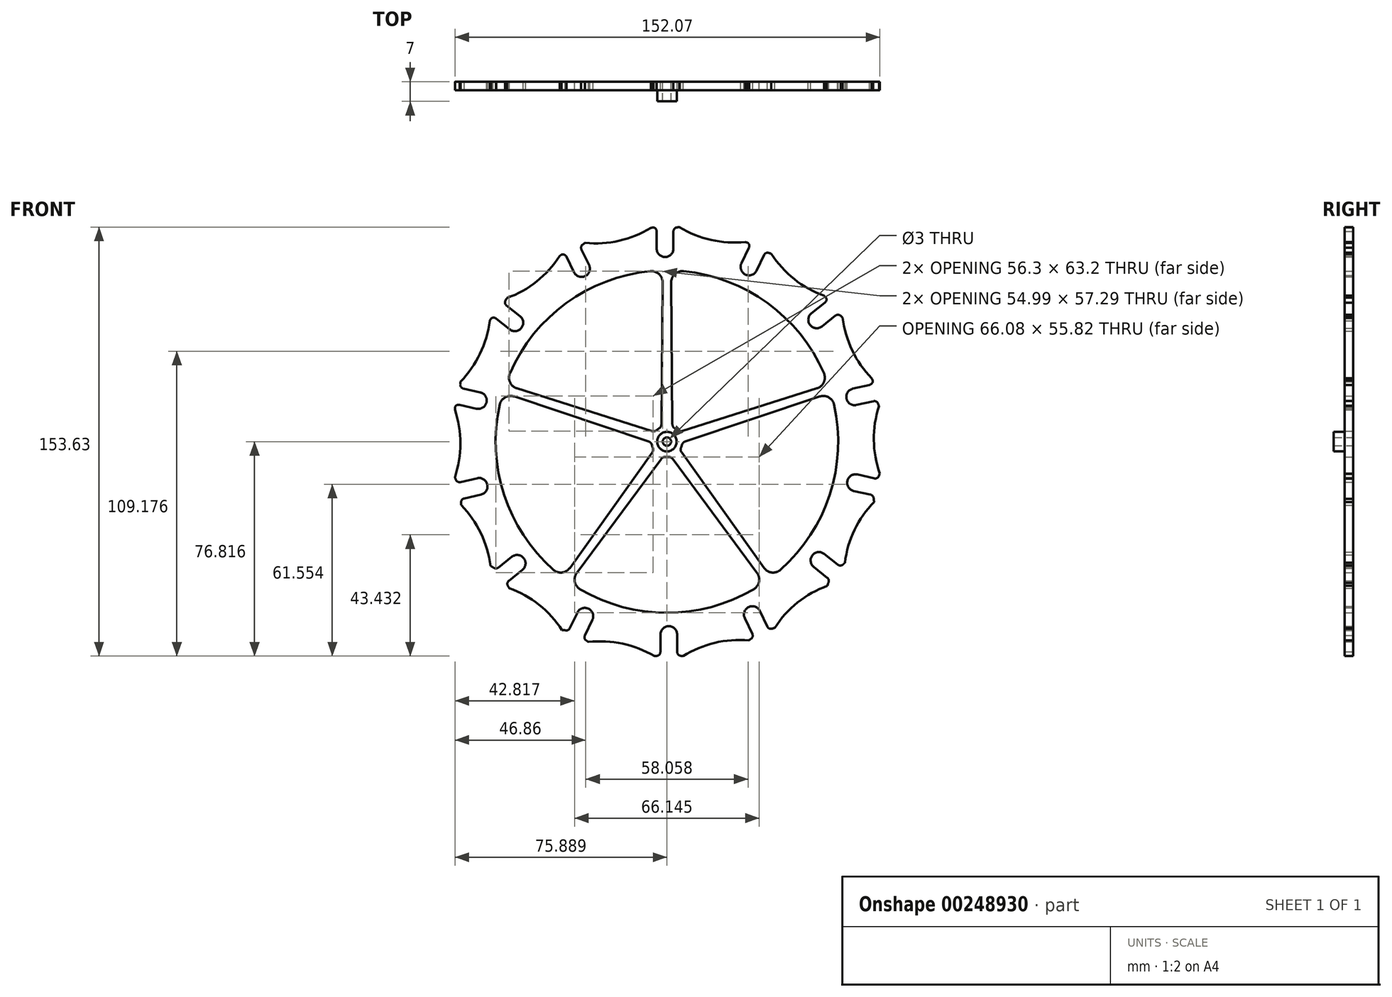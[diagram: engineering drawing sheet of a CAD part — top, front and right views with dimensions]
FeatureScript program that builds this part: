
annotation { "Feature Type Name" : "Feature", "Feature Type Description" : "" }
export const myFeature = defineFeature(function(context is Context, id is Id, definition is map)
    precondition{}
    {
        {
            var Q0;
            Q0=qCreatedBy(makeId("Front.planeOp"),FACE);
            var sketch = newSketch(context, id + "F0", { "sketchPlane" : qUnion([Q0])});
            skCircle(sketch, "E0", {"center": v(-22.2, -31.98) * mm, "radius": 2 * mm});
            skCircle(sketch, "E1", {"center": v(-22.2, -71.34) * mm, "radius": 1.5 * mm});
            skPoint(sketch, "E2.startSnap0", {"position": v(-22.24, -28.34) * mm});
            skPoint(sketch, "E3.orphan", {"position": v(-21.48, -28.34) * mm});
            skCircle(sketch, "E4", {"center": v(-22.2, -71.34) * mm, "radius": 2.5 * mm});
            skArc(sketch, "E5", {"start": v(-26.44, -36.03) * mm, "mid": v(-26.89, -36.09) * mm, "end": v(-27.34, -36.15) * mm});
            skArc(sketch, "E6.1.1", {"start": v(7.2, -29.99) * mm, "mid": v(6.81, -30.23) * mm, "end": v(6.43, -30.49) * mm});
            skArc(sketch, "E6.2.1", {"start": v(34.87, -9.95) * mm, "mid": v(34.73, -10.46) * mm, "end": v(34.6, -10.96) * mm});
            skArc(sketch, "E6.4.1", {"start": v(52.7, 54.24) * mm, "mid": v(52.87, 53.82) * mm, "end": v(53.03, 53.4) * mm});
            skPoint(sketch, "E6.center", {"position": v(-22.86, 40.67) * mm});
            skLineSegment(sketch, "E7", {"start": v(-25.2, -28.42) * mm, "end": v(-25.2, -34.62) * mm});
            skLineSegment(sketch, "E8.MirrorCS", {"start": v(-19.2, -28.42) * mm, "end": v(-19.2, -34.6) * mm});
            skArc(sketch, "E9", {"start": v(-19.2, -28.42) * mm, "mid": v(-22.2, -25.42) * mm, "end": v(-25.2, -28.42) * mm});
            skPoint(sketch, "E10.orphan", {"position": v(-25.2, -27.08) * mm});
            skPoint(sketch, "E11.orphan", {"position": v(-19.2, -27.02) * mm});
            skArc(sketch, "E12", {"start": v(-26.44, -36.03) * mm, "mid": v(-25.55, -35.56) * mm, "end": v(-25.2, -34.62) * mm});
            skPoint(sketch, "E13.orphan", {"position": v(-25.2, -35.93) * mm});
            skArc(sketch, "E14.MirrorCS", {"start": v(-17.94, -36.03) * mm, "mid": v(-18.84, -35.55) * mm, "end": v(-19.2, -34.6) * mm});
            skArc(sketch, "E15.1.0", {"start": v(10.42, -19.99) * mm, "mid": v(6.42, -18.59) * mm, "end": v(5.02, -22.6) * mm});
            skLineSegment(sketch, "E15.1.1", {"start": v(5.02, -22.6) * mm, "end": v(7.7, -28.18) * mm});
            skArc(sketch, "E15.1.2", {"start": v(7.2, -29.99) * mm, "mid": v(7.8, -29.18) * mm, "end": v(7.7, -28.18) * mm});
            skArc(sketch, "E15.1.3", {"start": v(14.85, -26.3) * mm, "mid": v(13.83, -26.26) * mm, "end": v(13.1, -25.55) * mm});
            skLineSegment(sketch, "E15.1.4", {"start": v(10.42, -19.99) * mm, "end": v(13.1, -25.55) * mm});
            skArc(sketch, "E15.2.0", {"start": v(33.44, 0.46) * mm, "mid": v(29.23, -0.01) * mm, "end": v(29.7, -4.23) * mm});
            skLineSegment(sketch, "E15.2.1", {"start": v(29.7, -4.23) * mm, "end": v(34.55, -8.1) * mm});
            skArc(sketch, "E15.2.2", {"start": v(34.87, -9.95) * mm, "mid": v(35.06, -8.96) * mm, "end": v(34.55, -8.1) * mm});
            skArc(sketch, "E15.2.3", {"start": v(40.17, -3.3) * mm, "mid": v(39.23, -3.72) * mm, "end": v(38.27, -3.39) * mm});
            skLineSegment(sketch, "E15.2.4", {"start": v(33.44, 0.46) * mm, "end": v(38.27, -3.39) * mm});
            skArc(sketch, "E15.3.0", {"start": v(45.31, 28.87) * mm, "mid": v(41.72, 26.61) * mm, "end": v(43.98, 23.02) * mm});
            skLineSegment(sketch, "E15.3.1", {"start": v(43.98, 23.02) * mm, "end": v(50.02, 21.64) * mm});
            skArc(sketch, "E15.3.2", {"start": v(51.12, 20.11) * mm, "mid": v(50.86, 21.08) * mm, "end": v(50.02, 21.64) * mm});
            skArc(sketch, "E15.3.3", {"start": v(53, 28.4) * mm, "mid": v(52.34, 27.62) * mm, "end": v(51.33, 27.5) * mm});
            skLineSegment(sketch, "E15.3.4", {"start": v(45.31, 28.87) * mm, "end": v(51.33, 27.5) * mm});
            skArc(sketch, "E15.4.0", {"start": v(43.68, 59.62) * mm, "mid": v(41.42, 56.02) * mm, "end": v(45.01, 53.77) * mm});
            skLineSegment(sketch, "E15.4.1", {"start": v(45.01, 53.77) * mm, "end": v(51.06, 55.15) * mm});
            skArc(sketch, "E15.4.2", {"start": v(52.7, 54.24) * mm, "mid": v(52.06, 55) * mm, "end": v(51.06, 55.15) * mm});
            skArc(sketch, "E15.4.3", {"start": v(50.82, 62.53) * mm, "mid": v(50.55, 61.54) * mm, "end": v(49.7, 61) * mm});
            skLineSegment(sketch, "E15.4.4", {"start": v(43.68, 59.62) * mm, "end": v(49.7, 61) * mm});
            skArc(sketch, "E15.5.0", {"start": v(28.87, 86.6) * mm, "mid": v(28.4, 82.4) * mm, "end": v(32.6, 81.92) * mm});
            skLineSegment(sketch, "E15.5.1", {"start": v(32.6, 81.92) * mm, "end": v(37.46, 85.79) * mm});
            skArc(sketch, "E15.5.2", {"start": v(39.33, 85.69) * mm, "mid": v(38.41, 86.1) * mm, "end": v(37.46, 85.79) * mm});
            skArc(sketch, "E15.5.3", {"start": v(34.04, 92.33) * mm, "mid": v(34.23, 91.33) * mm, "end": v(33.7, 90.46) * mm});
            skLineSegment(sketch, "E15.5.4", {"start": v(28.87, 86.6) * mm, "end": v(33.7, 90.46) * mm});
            skArc(sketch, "E15.6.0", {"start": v(3.8, 104.5) * mm, "mid": v(5.2, 100.5) * mm, "end": v(9.21, 101.9) * mm});
            skLineSegment(sketch, "E15.6.1", {"start": v(9.21, 101.9) * mm, "end": v(11.9, 107.49) * mm});
            skArc(sketch, "E15.6.2", {"start": v(13.64, 108.21) * mm, "mid": v(12.63, 108.18) * mm, "end": v(11.9, 107.49) * mm});
            skArc(sketch, "E15.6.3", {"start": v(5.99, 111.9) * mm, "mid": v(6.6, 111.08) * mm, "end": v(6.49, 110.06) * mm});
            skLineSegment(sketch, "E15.6.4", {"start": v(3.8, 104.5) * mm, "end": v(6.49, 110.06) * mm});
            skArc(sketch, "E15.7.0", {"start": v(-26.53, 109.75) * mm, "mid": v(-23.53, 106.75) * mm, "end": v(-20.53, 109.75) * mm});
            skLineSegment(sketch, "E15.7.1", {"start": v(-20.53, 109.75) * mm, "end": v(-20.53, 115.96) * mm});
            skArc(sketch, "E15.7.2", {"start": v(-19.28, 117.36) * mm, "mid": v(-20.17, 116.9) * mm, "end": v(-20.53, 115.96) * mm});
            skArc(sketch, "E15.7.3", {"start": v(-27.78, 117.36) * mm, "mid": v(-26.88, 116.88) * mm, "end": v(-26.53, 115.92) * mm});
            skLineSegment(sketch, "E15.7.4", {"start": v(-26.53, 109.75) * mm, "end": v(-26.53, 115.92) * mm});
            skArc(sketch, "E15.8.0", {"start": v(-56.14, 101.32) * mm, "mid": v(-52.14, 99.92) * mm, "end": v(-50.74, 103.92) * mm});
            skLineSegment(sketch, "E15.8.1", {"start": v(-50.74, 103.92) * mm, "end": v(-53.43, 109.51) * mm});
            skArc(sketch, "E15.8.2", {"start": v(-52.92, 111.32) * mm, "mid": v(-53.51, 110.51) * mm, "end": v(-53.43, 109.51) * mm});
            skArc(sketch, "E15.8.3", {"start": v(-60.57, 107.63) * mm, "mid": v(-59.55, 107.6) * mm, "end": v(-58.82, 106.88) * mm});
            skLineSegment(sketch, "E15.8.4", {"start": v(-56.14, 101.32) * mm, "end": v(-58.82, 106.88) * mm});
            skArc(sketch, "E15.9.0", {"start": v(-79.16, 80.87) * mm, "mid": v(-74.95, 81.35) * mm, "end": v(-75.42, 85.56) * mm});
            skLineSegment(sketch, "E15.9.1", {"start": v(-75.42, 85.56) * mm, "end": v(-80.27, 89.43) * mm});
            skArc(sketch, "E15.9.2", {"start": v(-80.6, 91.28) * mm, "mid": v(-80.78, 90.3) * mm, "end": v(-80.27, 89.43) * mm});
            skArc(sketch, "E15.9.3", {"start": v(-85.9, 84.64) * mm, "mid": v(-84.95, 85.05) * mm, "end": v(-83.99, 84.72) * mm});
            skLineSegment(sketch, "E15.9.4", {"start": v(-79.16, 80.87) * mm, "end": v(-83.99, 84.72) * mm});
            skArc(sketch, "E15.10.0", {"start": v(-91.03, 52.46) * mm, "mid": v(-87.44, 54.72) * mm, "end": v(-89.7, 58.31) * mm});
            skLineSegment(sketch, "E15.10.1", {"start": v(-89.7, 58.31) * mm, "end": v(-95.74, 59.7) * mm});
            skArc(sketch, "E15.10.2", {"start": v(-96.84, 61.22) * mm, "mid": v(-96.58, 60.25) * mm, "end": v(-95.74, 59.7) * mm});
            skArc(sketch, "E15.10.3", {"start": v(-98.73, 52.94) * mm, "mid": v(-98.06, 53.7) * mm, "end": v(-97.05, 53.83) * mm});
            skLineSegment(sketch, "E15.10.4", {"start": v(-91.03, 52.46) * mm, "end": v(-97.05, 53.83) * mm});
            skArc(sketch, "E15.11.0", {"start": v(-89.4, 21.71) * mm, "mid": v(-87.14, 25.3) * mm, "end": v(-90.73, 27.56) * mm});
            skLineSegment(sketch, "E15.11.1", {"start": v(-90.73, 27.56) * mm, "end": v(-96.78, 26.18) * mm});
            skArc(sketch, "E15.11.2", {"start": v(-98.43, 27.09) * mm, "mid": v(-97.78, 26.32) * mm, "end": v(-96.78, 26.18) * mm});
            skArc(sketch, "E15.11.3", {"start": v(-96.54, 18.8) * mm, "mid": v(-96.27, 19.79) * mm, "end": v(-95.42, 20.34) * mm});
            skLineSegment(sketch, "E15.11.4", {"start": v(-89.4, 21.71) * mm, "end": v(-95.42, 20.34) * mm});
            skArc(sketch, "E15.12.0", {"start": v(-74.59, -5.28) * mm, "mid": v(-74.11, -1.06) * mm, "end": v(-78.33, -0.59) * mm});
            skLineSegment(sketch, "E15.12.1", {"start": v(-78.33, -0.59) * mm, "end": v(-83.18, -4.46) * mm});
            skArc(sketch, "E15.12.2", {"start": v(-85.05, -4.36) * mm, "mid": v(-84.13, -4.76) * mm, "end": v(-83.18, -4.46) * mm});
            skArc(sketch, "E15.12.3", {"start": v(-79.76, -11) * mm, "mid": v(-79.95, -10) * mm, "end": v(-79.41, -9.13) * mm});
            skLineSegment(sketch, "E15.12.4", {"start": v(-74.59, -5.28) * mm, "end": v(-79.41, -9.13) * mm});
            skArc(sketch, "E15.13.0", {"start": v(-49.53, -23.17) * mm, "mid": v(-50.93, -19.17) * mm, "end": v(-54.94, -20.57) * mm});
            skLineSegment(sketch, "E15.13.1", {"start": v(-54.94, -20.57) * mm, "end": v(-57.63, -26.16) * mm});
            skArc(sketch, "E15.13.2", {"start": v(-59.36, -26.88) * mm, "mid": v(-58.36, -26.85) * mm, "end": v(-57.63, -26.16) * mm});
            skArc(sketch, "E15.13.3", {"start": v(-51.7, -30.57) * mm, "mid": v(-52.31, -29.75) * mm, "end": v(-52.2, -28.73) * mm});
            skLineSegment(sketch, "E15.13.4", {"start": v(-49.53, -23.17) * mm, "end": v(-52.2, -28.73) * mm});
            skPoint(sketch, "E16.trimOffspring.start.orphan", {"position": v(-19.2, -35.87) * mm});
            skPoint(sketch, "E17.orphan", {"position": v(-11.1, -37.55) * mm});
            skArc(sketch, "E18.trimOffspring", {"start": v(6.43, -30.49) * mm, "mid": v(-5.77, -31.4) * mm, "end": v(-17.04, -36.15) * mm});
            skArc(sketch, "E19.trimOffspring", {"start": v(15.71, -26.02) * mm, "mid": v(15.28, -26.16) * mm, "end": v(14.85, -26.3) * mm});
            skArc(sketch, "E20.trimOffspring", {"start": v(34.6, -10.96) * mm, "mid": v(23.92, -16.95) * mm, "end": v(15.71, -26.02) * mm});
            skArc(sketch, "E21.trimOffspring", {"start": v(40.83, -2.68) * mm, "mid": v(40.5, -3) * mm, "end": v(40.17, -3.3) * mm});
            skArc(sketch, "E22.trimOffspring", {"start": v(51.12, 20.11) * mm, "mid": v(51.2, 19.6) * mm, "end": v(51.3, 19.08) * mm});
            skArc(sketch, "E23.trimOffspring", {"start": v(53.32, 29.25) * mm, "mid": v(53.16, 28.82) * mm, "end": v(53, 28.4) * mm});
            skArc(sketch, "E24.trimOffspring", {"start": v(51.3, 19.08) * mm, "mid": v(44.29, 9.05) * mm, "end": v(40.83, -2.68) * mm});
            skArc(sketch, "E25.trimOffspring", {"start": v(53.03, 53.4) * mm, "mid": v(51.2, 41.3) * mm, "end": v(53.32, 29.25) * mm});
            skArc(sketch, "E26.trimOffspring", {"start": v(50.47, 63.3) * mm, "mid": v(50.64, 62.91) * mm, "end": v(50.82, 62.53) * mm});
            skArc(sketch, "E27.trimOffspring", {"start": v(39.99, 85.06) * mm, "mid": v(43.45, 73.32) * mm, "end": v(50.47, 63.3) * mm});
            skArc(sketch, "E28.trimOffspring", {"start": v(33.38, 92.88) * mm, "mid": v(33.7, 92.6) * mm, "end": v(34.04, 92.33) * mm});
            skArc(sketch, "E29.trimOffspring", {"start": v(13.64, 108.21) * mm, "mid": v(14.07, 108.07) * mm, "end": v(14.5, 107.93) * mm});
            skArc(sketch, "E30.trimOffspring", {"start": v(14.5, 107.93) * mm, "mid": v(22.71, 98.86) * mm, "end": v(33.38, 92.88) * mm});
            skArc(sketch, "E31.trimOffspring", {"start": v(5.16, 112.1) * mm, "mid": v(5.57, 112) * mm, "end": v(5.99, 111.9) * mm});
            skArc(sketch, "E32.trimOffspring", {"start": v(-19.28, 117.36) * mm, "mid": v(-18.83, 117.42) * mm, "end": v(-18.38, 117.48) * mm});
            skArc(sketch, "E33.trimOffspring", {"start": v(-18.38, 117.48) * mm, "mid": v(-7.05, 112.87) * mm, "end": v(5.16, 112.1) * mm});
            skArc(sketch, "E34.trimOffspring", {"start": v(-28.61, 117.2) * mm, "mid": v(-28.2, 117.27) * mm, "end": v(-27.78, 117.36) * mm});
            skArc(sketch, "E35.trimOffspring", {"start": v(-52.92, 111.32) * mm, "mid": v(-52.53, 111.57) * mm, "end": v(-52.15, 111.82) * mm});
            skArc(sketch, "E36.trimOffspring", {"start": v(-52.15, 111.82) * mm, "mid": v(-39.95, 112.58) * mm, "end": v(-28.61, 117.2) * mm});
            skArc(sketch, "E37.trimOffspring", {"start": v(-61.25, 107.12) * mm, "mid": v(-60.9, 107.37) * mm, "end": v(-60.57, 107.63) * mm});
            skArc(sketch, "E38.trimOffspring", {"start": v(-80.6, 91.28) * mm, "mid": v(-80.36, 91.67) * mm, "end": v(-80.13, 92.06) * mm});
            skArc(sketch, "E39.trimOffspring", {"start": v(-80.13, 92.06) * mm, "mid": v(-69.46, 98.05) * mm, "end": v(-61.25, 107.12) * mm});
            skArc(sketch, "E40.trimOffspring", {"start": v(-86.28, 83.88) * mm, "mid": v(-86.08, 84.26) * mm, "end": v(-85.9, 84.64) * mm});
            skArc(sketch, "E41.trimOffspring", {"start": v(-96.84, 61.22) * mm, "mid": v(-96.8, 61.67) * mm, "end": v(-96.75, 62.13) * mm});
            skArc(sketch, "E42.trimOffspring", {"start": v(-96.75, 62.13) * mm, "mid": v(-89.74, 72.15) * mm, "end": v(-86.28, 83.88) * mm});
            skArc(sketch, "E43.trimOffspring", {"start": v(-98.75, 52.09) * mm, "mid": v(-98.74, 52.51) * mm, "end": v(-98.73, 52.94) * mm});
            skArc(sketch, "E44.trimOffspring", {"start": v(-98.43, 27.09) * mm, "mid": v(-98.59, 27.51) * mm, "end": v(-98.75, 27.94) * mm});
            skArc(sketch, "E45.trimOffspring", {"start": v(-98.75, 27.94) * mm, "mid": v(-96.78, 40.01) * mm, "end": v(-98.75, 52.09) * mm});
            skArc(sketch, "E46.trimOffspring", {"start": v(-96.46, 17.9) * mm, "mid": v(-96.5, 18.35) * mm, "end": v(-96.54, 18.8) * mm});
            skArc(sketch, "E47.trimOffspring", {"start": v(-85.05, -4.36) * mm, "mid": v(-85.52, -4.1) * mm, "end": v(-85.98, -3.86) * mm});
            skArc(sketch, "E48.trimOffspring", {"start": v(-85.98, -3.86) * mm, "mid": v(-89.44, 7.88) * mm, "end": v(-96.46, 17.9) * mm});
            skArc(sketch, "E49.trimOffspring", {"start": v(-79.29, -11.78) * mm, "mid": v(-79.52, -11.39) * mm, "end": v(-79.76, -11) * mm});
            skArc(sketch, "E50.trimOffspring", {"start": v(-60.41, -26.83) * mm, "mid": v(-68.62, -17.76) * mm, "end": v(-79.29, -11.78) * mm});
            skArc(sketch, "E51.trimOffspring", {"start": v(-59.36, -26.88) * mm, "mid": v(-59.89, -26.85) * mm, "end": v(-60.41, -26.83) * mm});
            skArc(sketch, "E52.trimOffspring", {"start": v(-50.95, -31.07) * mm, "mid": v(-51.33, -30.82) * mm, "end": v(-51.7, -30.57) * mm});
            skArc(sketch, "E53.trimOffspring", {"start": v(-27.34, -36.15) * mm, "mid": v(-38.73, -31.68) * mm, "end": v(-50.95, -31.07) * mm});
            skArc(sketch, "E54.trimOffspring", {"start": v(-17.04, -36.15) * mm, "mid": v(-17.5, -36.09) * mm, "end": v(-17.94, -36.03) * mm});
            skPoint(sketch, "E55.orphan", {"position": v(-33.29, -37.55) * mm});
            skLineSegment(sketch, "E56", {"start": v(39.33, 85.69) * mm, "end": v(39.99, 85.06) * mm});
            skCircle(sketch, "E57", {"center": v(-22.86, 40.67) * mm, "radius": 1.5 * mm});
            skCircle(sketch, "E58", {"center": v(-22.86, 40.67) * mm, "radius": 3.5 * mm});
            skArc(sketch, "E59", {"start": v(-28.22, 39.42) * mm, "mid": v(-28.1, 38.97) * mm, "end": v(-27.93, 38.53) * mm});
            skLineSegment(sketch, "E60", {"start": v(-23.53, 110.93) * mm, "end": v(-23.53, 109.75) * mm});
            skArc(sketch, "E61", {"start": v(-82.71, 53.89) * mm, "mid": v(-81.15, 21.73) * mm, "end": v(-63.5, -5.2) * mm});
            skLineSegment(sketch, "E62", {"start": v(-24.82, 46.93) * mm, "end": v(-24.4, 97.66) * mm});
            skLineSegment(sketch, "E63.trimOffspring", {"start": v(-23.53, 109.75) * mm, "end": v(-23.53, 110.93) * mm});
            skLineSegment(sketch, "E64.MirrorCS", {"start": v(-20.9, 46.93) * mm, "end": v(-21.33, 97.66) * mm});
            skLineSegment(sketch, "E65.MirrorCS", {"start": v(-20.74, 35.68) * mm, "end": v(-20.74, 35.6) * mm});
            skLineSegment(sketch, "E66.MirrorCS", {"start": v(-24.67, 35.56) * mm, "end": v(-24.67, 35.47) * mm});
            skLineSegment(sketch, "E67.trimOffspring", {"start": v(-22.2, -25.42) * mm, "end": v(-22.2, -31.98) * mm});
            skPoint(sketch, "E68.orphan", {"position": v(-19.51, -20.45) * mm});
            skLineSegment(sketch, "E69.trimOffspring", {"start": v(20.48, -2.67) * mm, "end": v(21.12, -3.31) * mm});
            skPoint(sketch, "E70.orphan", {"position": v(-8.62, 26.42) * mm});
            skPoint(sketch, "E71.orphan", {"position": v(-38.44, 26.42) * mm});
            skArc(sketch, "E72", {"start": v(-20.9, 46.93) * mm, "mid": v(-20.66, 46.04) * mm, "end": v(-20.02, 45.37) * mm});
            skPoint(sketch, "E73.orphan", {"position": v(-20.9, 45.8) * mm});
            skArc(sketch, "E74.MirrorCS", {"start": v(-24.82, 46.93) * mm, "mid": v(-25.06, 46.04) * mm, "end": v(-25.7, 45.37) * mm});
            skPoint(sketch, "E75.orphan", {"position": v(-24.83, 45.8) * mm});
            skArc(sketch, "E76", {"start": v(-16.94, 101.67) * mm, "mid": v(-20.03, 100.64) * mm, "end": v(-21.33, 97.66) * mm});
            skPoint(sketch, "E77.orphan", {"position": v(-21.36, 101.94) * mm});
            skArc(sketch, "E78.MirrorCS", {"start": v(-28.78, 101.67) * mm, "mid": v(-25.7, 100.64) * mm, "end": v(-24.4, 97.66) * mm});
            skPoint(sketch, "E79.orphan", {"position": v(-24.36, 101.94) * mm});
            skArc(sketch, "E80.1.0", {"start": v(-82.71, 53.89) * mm, "mid": v(-80.78, 56.5) * mm, "end": v(-77.54, 56.82) * mm});
            skArc(sketch, "E80.1.1", {"start": v(-79.05, 65.15) * mm, "mid": v(-79.02, 61.9) * mm, "end": v(-76.59, 59.74) * mm});
            skLineSegment(sketch, "E80.1.2", {"start": v(-28.21, 44.46) * mm, "end": v(-76.59, 59.74) * mm});
            skLineSegment(sketch, "E80.1.3", {"start": v(-29.42, 40.74) * mm, "end": v(-77.54, 56.82) * mm});
            skArc(sketch, "E80.1.4", {"start": v(-29.42, 40.74) * mm, "mid": v(-28.65, 40.23) * mm, "end": v(-28.22, 39.42) * mm});
            skArc(sketch, "E80.1.5", {"start": v(-28.21, 44.46) * mm, "mid": v(-27.29, 44.42) * mm, "end": v(-26.46, 44.82) * mm});
            skArc(sketch, "E80.2.0", {"start": v(-53.93, -12.17) * mm, "mid": v(-55.82, -9.52) * mm, "end": v(-55.12, -6.34) * mm});
            skArc(sketch, "E80.2.1", {"start": v(-63.5, -5.2) * mm, "mid": v(-60.4, -6.19) * mm, "end": v(-57.6, -4.54) * mm});
            skLineSegment(sketch, "E80.2.2", {"start": v(-28.13, 36.75) * mm, "end": v(-57.6, -4.54) * mm});
            skLineSegment(sketch, "E80.2.3", {"start": v(-24.96, 34.45) * mm, "end": v(-55.12, -6.34) * mm});
            skArc(sketch, "E80.2.4", {"start": v(-24.96, 34.45) * mm, "mid": v(-24.24, 35.03) * mm, "end": v(-23.33, 35.19) * mm});
            skArc(sketch, "E80.2.5", {"start": v(-28.13, 36.75) * mm, "mid": v(-27.8, 37.61) * mm, "end": v(-27.93, 38.53) * mm});
            skArc(sketch, "E81.4.3.0", {"start": v(8.2, -12.17) * mm, "mid": v(10.1, -9.52) * mm, "end": v(9.4, -6.34) * mm});
            skLineSegment(sketch, "E81.8.3.0", {"start": v(-20.76, 34.45) * mm, "end": v(9.4, -6.34) * mm});
            skLineSegment(sketch, "E81.11.3.0", {"start": v(-17.6, 36.75) * mm, "end": v(11.88, -4.54) * mm});
            skArc(sketch, "E81.14.3.0", {"start": v(-17.6, 36.75) * mm, "mid": v(-17.93, 37.61) * mm, "end": v(-17.8, 38.53) * mm});
            skArc(sketch, "E81.17.3.0", {"start": v(17.79, -5.2) * mm, "mid": v(14.69, -6.19) * mm, "end": v(11.88, -4.54) * mm});
            skArc(sketch, "E81.18.3.0", {"start": v(-20.76, 34.45) * mm, "mid": v(-21.48, 35.03) * mm, "end": v(-22.4, 35.19) * mm});
            skArc(sketch, "E81.4.4.0", {"start": v(36.99, 53.89) * mm, "mid": v(35.06, 56.5) * mm, "end": v(31.82, 56.82) * mm});
            skLineSegment(sketch, "E81.8.4.0", {"start": v(-16.3, 40.74) * mm, "end": v(31.82, 56.82) * mm});
            skLineSegment(sketch, "E81.11.4.0", {"start": v(-17.5, 44.46) * mm, "end": v(30.87, 59.74) * mm});
            skArc(sketch, "E81.14.4.0", {"start": v(-17.5, 44.46) * mm, "mid": v(-18.43, 44.42) * mm, "end": v(-19.26, 44.82) * mm});
            skArc(sketch, "E81.17.4.0", {"start": v(33.33, 65.15) * mm, "mid": v(33.3, 61.9) * mm, "end": v(30.87, 59.74) * mm});
            skArc(sketch, "E81.18.4.0", {"start": v(-16.3, 40.74) * mm, "mid": v(-17.07, 40.23) * mm, "end": v(-17.5, 39.42) * mm});
            skArc(sketch, "E82.trimOffspring", {"start": v(33.33, 65.15) * mm, "mid": v(13.17, 90.25) * mm, "end": v(-16.94, 101.67) * mm});
            skPoint(sketch, "E83.MirrorCS.start.orphan", {"position": v(20.43, 85.3) * mm});
            skPoint(sketch, "E84.start.orphan", {"position": v(-67.5, 85.3) * mm});
            skArc(sketch, "E85.trimOffspring", {"start": v(-28.78, 101.67) * mm, "mid": v(-58.89, 90.25) * mm, "end": v(-79.05, 65.15) * mm});
            skPoint(sketch, "E86.trimOffspring.end.orphan", {"position": v(-22.86, 46.17) * mm});
            skArc(sketch, "E87.trimOffspring", {"start": v(17.79, -5.2) * mm, "mid": v(35.43, 21.73) * mm, "end": v(36.99, 53.89) * mm});
            skArc(sketch, "E88.trimOffspring", {"start": v(-53.93, -12.17) * mm, "mid": v(-22.86, -20.63) * mm, "end": v(8.2, -12.17) * mm});
            skPoint(sketch, "E89.orphan", {"position": v(-22.86, 101.96) * mm});
            skArc(sketch, "E90.trimOffspring", {"start": v(-23.33, 35.19) * mm, "mid": v(-22.86, 35.17) * mm, "end": v(-22.4, 35.19) * mm});
            skArc(sketch, "E91.trimOffspring", {"start": v(-17.8, 38.53) * mm, "mid": v(-17.63, 38.97) * mm, "end": v(-17.5, 39.42) * mm});
            skArc(sketch, "E92.trimOffspring", {"start": v(-19.26, 44.82) * mm, "mid": v(-19.63, 45.12) * mm, "end": v(-20.02, 45.37) * mm});
            skArc(sketch, "E93.trimOffspring", {"start": v(-25.7, 45.37) * mm, "mid": v(-26.1, 45.12) * mm, "end": v(-26.46, 44.82) * mm});
            skCircle(sketch, "E94", {"center": v(-22.86, 40.67) * mm, "radius": 112 * mm, "construction": true});
            skLineSegment(sketch, "E95", {"start": v(-98.75, 27.94) * mm, "end": v(-96.46, 17.9) * mm, "construction": true});
            skLineSegment(sketch, "E96", {"start": v(-98.75, 52.09) * mm, "end": v(53.32, 29.25) * mm, "construction": true});
            skCircle(sketch, "E97", {"center": v(-22.2, -71.34) * mm, "radius": 24.66 * mm, "construction": true});
            skCircle(sketch, "E98", {"center": v(-22.2, -71.34) * mm, "radius": 35.56 * mm, "construction": true});
            skSolve(sketch);
        }
        {
            var Q0;
            Q0=makeQuery(id+"F0.imprint","IMPRINT",FACE,{"disambiguationData":[TD([[makeQuery(id+"F0.imprint","IMPRINT",EDGE,{"derivedFrom":sQuery(id+"F0.wireOp",EDGE,"E5")}),-1.0]])]});
            extrude(context, id + "F1", {"entities" : qUnion([Q0]), "depth" : 3 * mm});
        }
        {
            var Q0;
            Q0=makeQuery(id+"F0.imprint","IMPRINT",FACE,{"disambiguationData":[TD([[makeQuery(id+"F0.imprint","IMPRINT",EDGE,{"derivedFrom":sQuery(id+"F0.wireOp",EDGE,"E57")}),-1.0]])]});
            extrude(context, id + "F2", {"entities" : qUnion([Q0]), "operationType" : NewBodyOperationType.ADD, "depth" : 7 * mm});
        }
    });
